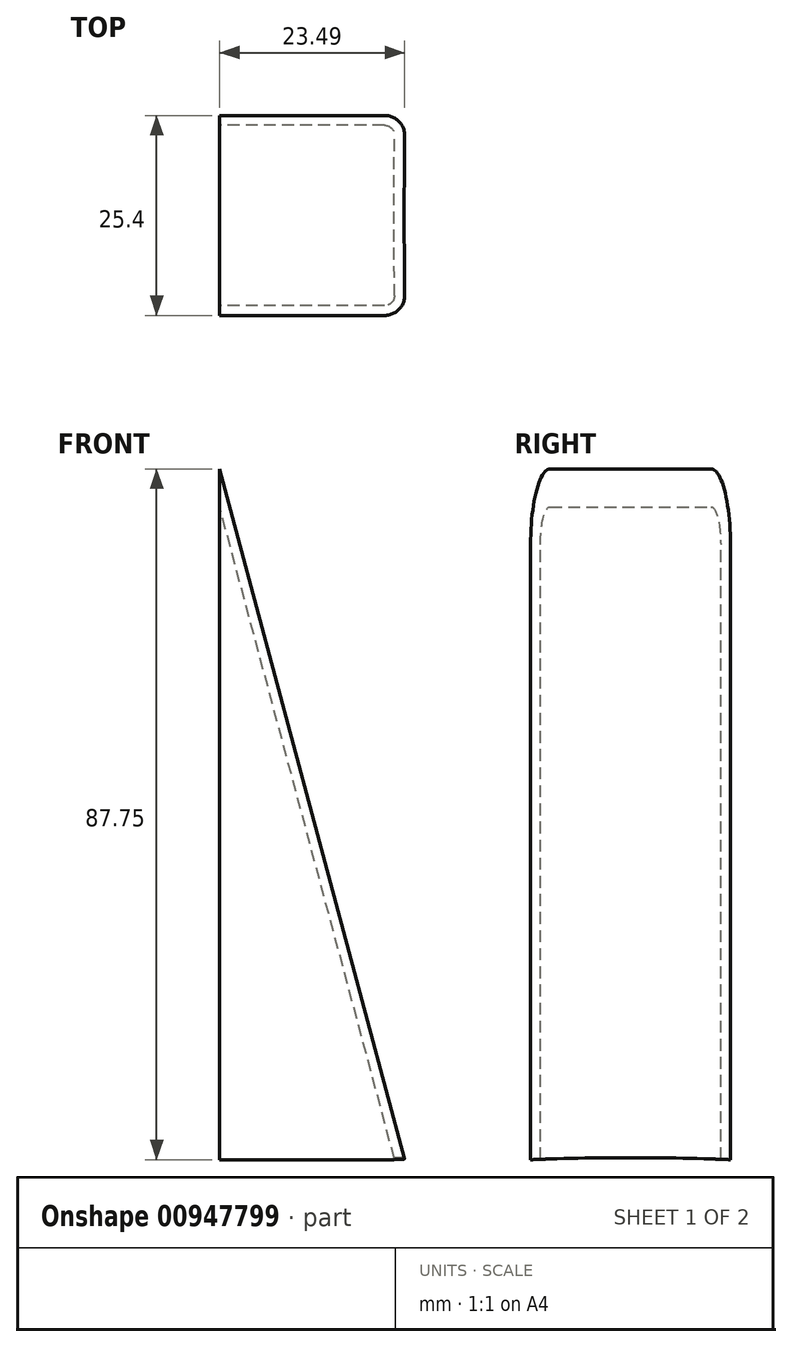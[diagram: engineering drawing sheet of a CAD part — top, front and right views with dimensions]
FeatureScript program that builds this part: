
annotation { "Feature Type Name" : "Feature", "Feature Type Description" : "" }
export const myFeature = defineFeature(function(context is Context, id is Id, definition is map)
    precondition{}
    {
        {
            var Q0;
            Q0=qCreatedBy(makeId("Top.planeOp"),FACE);
            var sketch = newSketch(context, id + "F0", { "sketchPlane" : qUnion([Q0])});
            skLineSegment(sketch, "E0", {"start": v(0, 0) * mm, "end": v(0, -56.17) * mm, "construction": true});
            skSolve(sketch);
        }
        {
            var Q0;
            Q0=qCreatedBy(makeId("Top.planeOp"),FACE);
            var Q1;
            Q1=sQuery(id+"F0.wireOp",EDGE,"E0");
            cPlane(context, id + "F1", {"entities" : qUnion([Q0, Q1]), "cplaneType" : CPlaneType.LINE_ANGLE, "offset" : 25 * mm, "angle" : 15 * degree, "width" : 150 * mm, "height" : 150 * mm});
        }
        {
            var Q0;
            Q0=qCreatedBy(id+"F1.planeOp",FACE);
            var sketch = newSketch(context, id + "F2", { "sketchPlane" : qUnion([Q0])});
            skLineSegment(sketch, "E1", {"start": v(0, 460.4) * mm, "end": v(0, -154.06) * mm, "construction": true});
            skLineSegment(sketch, "E2.bottom", {"start": v(10.21, -12.7) * mm, "end": v(-10.21, -12.7) * mm});
            skLineSegment(sketch, "E2.top", {"start": v(10.21, 12.7) * mm, "end": v(-10.21, 12.7) * mm});
            skLineSegment(sketch, "E2.left", {"start": v(12.7, -10.21) * mm, "end": v(12.7, 10.21) * mm});
            skLineSegment(sketch, "E2.right", {"start": v(-12.7, -10.21) * mm, "end": v(-12.7, 10.21) * mm});
            skPoint(sketch, "E2.middle", {"position": v(0, 0) * mm});
            skLineSegment(sketch, "E3.bottom", {"start": v(10.21, -11.46) * mm, "end": v(-10.21, -11.46) * mm});
            skLineSegment(sketch, "E3.top", {"start": v(10.21, 11.46) * mm, "end": v(-10.21, 11.46) * mm});
            skLineSegment(sketch, "E3.left", {"start": v(11.46, -10.21) * mm, "end": v(11.46, 10.21) * mm});
            skLineSegment(sketch, "E3.right", {"start": v(-11.46, -10.21) * mm, "end": v(-11.46, 10.21) * mm});
            skPoint(sketch, "E4.visualSharp", {"position": v(-11.46, 11.46) * mm});
            skArc(sketch, "E4.filletArc", {"start": v(-10.21, 11.46) * mm, "mid": v(-11.1, 11.1) * mm, "end": v(-11.46, 10.21) * mm});
            skPoint(sketch, "E5.visualSharp", {"position": v(11.46, 11.46) * mm});
            skArc(sketch, "E5.filletArc", {"start": v(11.46, 10.21) * mm, "mid": v(11.1, 11.1) * mm, "end": v(10.21, 11.46) * mm});
            skPoint(sketch, "E6.visualSharp", {"position": v(11.46, -11.46) * mm});
            skArc(sketch, "E6.filletArc", {"start": v(10.21, -11.46) * mm, "mid": v(11.1, -11.1) * mm, "end": v(11.46, -10.21) * mm});
            skPoint(sketch, "E7.visualSharp", {"position": v(-11.46, -11.46) * mm});
            skArc(sketch, "E7.filletArc", {"start": v(-11.46, -10.21) * mm, "mid": v(-11.1, -11.1) * mm, "end": v(-10.21, -11.46) * mm});
            skPoint(sketch, "E8.visualSharp", {"position": v(-12.7, 12.7) * mm});
            skArc(sketch, "E8.filletArc", {"start": v(-10.21, 12.7) * mm, "mid": v(-11.97, 11.97) * mm, "end": v(-12.7, 10.21) * mm});
            skPoint(sketch, "E9.visualSharp", {"position": v(12.7, 12.7) * mm});
            skArc(sketch, "E9.filletArc", {"start": v(12.7, 10.21) * mm, "mid": v(11.97, 11.97) * mm, "end": v(10.21, 12.7) * mm});
            skPoint(sketch, "E10.visualSharp", {"position": v(12.7, -12.7) * mm});
            skArc(sketch, "E10.filletArc", {"start": v(10.21, -12.7) * mm, "mid": v(11.97, -11.97) * mm, "end": v(12.7, -10.21) * mm});
            skPoint(sketch, "E11.visualSharp", {"position": v(-12.7, -12.7) * mm});
            skArc(sketch, "E11.filletArc", {"start": v(-12.7, -10.21) * mm, "mid": v(-11.97, -11.97) * mm, "end": v(-10.21, -12.7) * mm});
            skSolve(sketch);
        }
        {
            var Q0;
            Q0 = qSketchRegion(id + "F2", true);
            extrude(context, id + "F3", {"entities" : qUnion([Q0]), "depth" : 92.04 * mm, "offsetDistance" : 25 * mm});
        }
        {
            var Q0;
            Q0=qCreatedBy(makeId("Front.planeOp"),FACE);
            var sketch = newSketch(context, id + "F4", { "sketchPlane" : qUnion([Q0])});
            skLineSegment(sketch, "E12", {"start": v(12.27, 3.29) * mm, "end": v(12.27, -125.24) * mm});
            skLineSegment(sketch, "E13", {"start": v(12.27, 3.29) * mm, "end": v(-32.71, 3.29) * mm});
            skLineSegment(sketch, "E14", {"start": v(-32.71, 3.29) * mm, "end": v(-32.71, -125.24) * mm});
            skLineSegment(sketch, "E15", {"start": v(-32.71, -125.24) * mm, "end": v(12.27, -125.24) * mm});
            skSolve(sketch);
        }
        {
            var Q0;
            Q0 = qSketchRegion(id + "F4", true);
            extrude(context, id + "F5", {"entities" : qUnion([Q0]), "operationType" : NewBodyOperationType.REMOVE, "oppositeDirection" : true, "depth" : 50 * mm, "offsetDistance" : 25 * mm, "symmetric" : true});
        }
        {
            var Q0;
            Q0=qCreatedBy(makeId("Right.planeOp"),FACE);
            var sketch = newSketch(context, id + "F6", { "sketchPlane" : qUnion([Q0])});
            skLineSegment(sketch, "E16", {"start": v(0, 0) * mm, "end": v(0, -389) * mm, "construction": true});
            skArc(sketch, "E17", {"start": v(55.83, -89.36) * mm, "mid": v(2.08, -84.2) * mm, "end": v(-51.74, -88.62) * mm});
            skLineSegment(sketch, "E18", {"start": v(-51.74, -88.62) * mm, "end": v(0, -155.82) * mm});
            skLineSegment(sketch, "E19", {"start": v(0, -155.82) * mm, "end": v(55.83, -89.36) * mm});
            skSolve(sketch);
        }
        {
            var Q0;
            Q0 = qSketchRegion(id + "F6", true);
            extrude(context, id + "F7", {"entities" : qUnion([Q0]), "operationType" : NewBodyOperationType.REMOVE, "depth" : 50 * mm, "offsetDistance" : 25 * mm});
        }
    });
